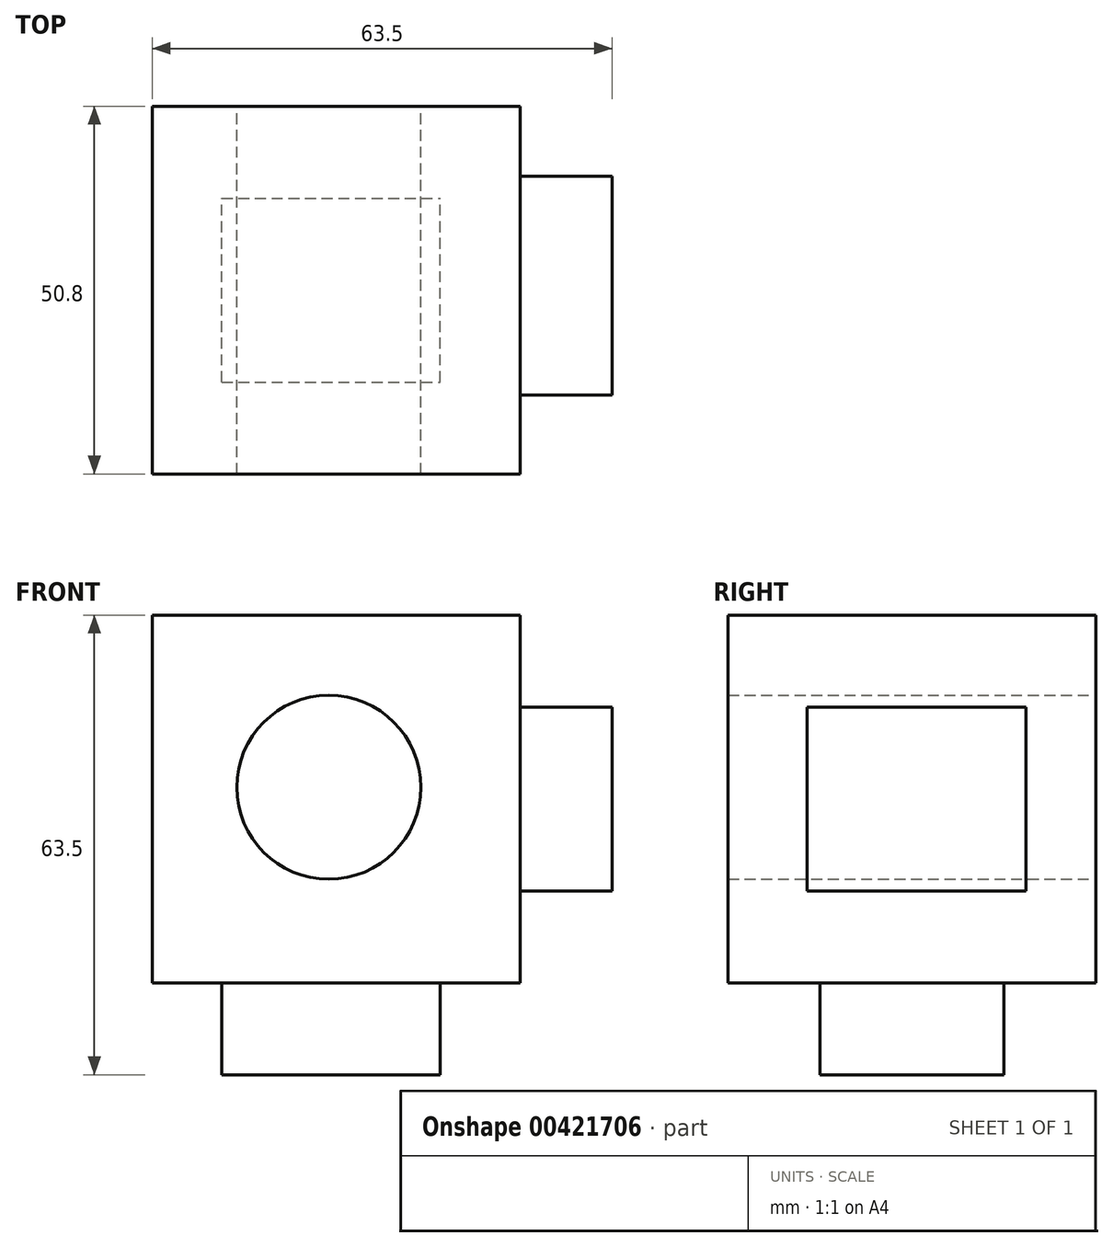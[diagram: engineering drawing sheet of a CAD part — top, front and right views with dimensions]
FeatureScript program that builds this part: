
annotation { "Feature Type Name" : "Feature", "Feature Type Description" : "" }
export const myFeature = defineFeature(function(context is Context, id is Id, definition is map)
    precondition{}
    {
        {
            var Q0;
            Q0=qCreatedBy(makeId("Front.planeOp"),FACE);
            var sketch = newSketch(context, id + "F0", { "sketchPlane" : qUnion([Q0])});
            skLineSegment(sketch, "E0.bottom", {"start": v(0, 0) * mm, "end": v(50.8, 0) * mm});
            skLineSegment(sketch, "E0.top", {"start": v(0, 50.8) * mm, "end": v(50.8, 50.8) * mm});
            skLineSegment(sketch, "E0.left", {"start": v(0, 0) * mm, "end": v(0, 50.8) * mm});
            skLineSegment(sketch, "E0.right", {"start": v(50.8, 0) * mm, "end": v(50.8, 50.8) * mm});
            skSolve(sketch);
        }
        {
            var Q0;
            Q0=makeQuery(id+"F0.imprint","IMPRINT",FACE,{"disambiguationData":[TD([[makeQuery(id+"F0.imprint","IMPRINT",EDGE,{"derivedFrom":sQuery(id+"F0.wireOp",EDGE,"E0.bottom")}),1.0]])]});
            var sketch = newSketch(context, id + "F1", { "sketchPlane" : qUnion([Q0])});
            skCircle(sketch, "E1", {"center": v(24.37, 27) * mm, "radius": 12.7 * mm});
            skSolve(sketch);
        }
        {
            var Q0;
            Q0=makeQuery(id+"F1.imprint","IMPRINT",FACE,{"disambiguationData":[TD([[makeQuery(id+"F1.imprint","IMPRINT",EDGE,{"derivedFrom":sQuery(id+"F1.wireOp",EDGE,"E1")}),-1.0]])]});
            extrude(context, id + "F2", {"entities" : qUnion([Q0]), "depth" : 50.8 * mm});
        }
        {
            var Q0;
            Q0=makeQuery(id+"F2.opExtrude","SWEPT_FACE",FACE,{"disambiguationData":[OSD([sQuery(id+"F0.wireOp",EDGE,"E0.bottom")])]});
            var sketch = newSketch(context, id + "F3", { "sketchPlane" : qUnion([Q0])});
            skLineSegment(sketch, "E2.bottom", {"start": v(9.6, 38.1) * mm, "end": v(39.75, 38.1) * mm});
            skLineSegment(sketch, "E2.top", {"start": v(9.6, 12.7) * mm, "end": v(39.75, 12.7) * mm});
            skLineSegment(sketch, "E2.left", {"start": v(9.6, 38.1) * mm, "end": v(9.6, 12.7) * mm});
            skLineSegment(sketch, "E2.right", {"start": v(39.75, 38.1) * mm, "end": v(39.75, 12.7) * mm});
            skSolve(sketch);
        }
        {
            var Q0;
            Q0=makeQuery(id+"F3.imprint","IMPRINT",FACE,{"disambiguationData":[TD([[makeQuery(id+"F3.imprint","IMPRINT",EDGE,{"derivedFrom":sQuery(id+"F3.wireOp",EDGE,"E2.bottom")}),-1.0]])]});
            extrude(context, id + "F4", {"entities" : qUnion([Q0]), "operationType" : NewBodyOperationType.ADD, "depth" : 12.7 * mm});
        }
        {
            var Q0;
            Q0=makeQuery(id+"F2.opExtrude","SWEPT_FACE",FACE,{"disambiguationData":[OSD([sQuery(id+"F0.wireOp",EDGE,"E0.right")])]});
            var sketch = newSketch(context, id + "F5", { "sketchPlane" : qUnion([Q0])});
            skLineSegment(sketch, "E3.bottom", {"start": v(-39.88, 38.1) * mm, "end": v(-9.67, 38.1) * mm});
            skLineSegment(sketch, "E3.top", {"start": v(-39.88, 12.7) * mm, "end": v(-9.67, 12.7) * mm});
            skLineSegment(sketch, "E3.left", {"start": v(-39.88, 38.1) * mm, "end": v(-39.88, 12.7) * mm});
            skLineSegment(sketch, "E3.right", {"start": v(-9.67, 38.1) * mm, "end": v(-9.67, 12.7) * mm});
            skSolve(sketch);
        }
        {
            var Q0;
            Q0=makeQuery(id+"F5.imprint","IMPRINT",FACE,{"disambiguationData":[TD([[makeQuery(id+"F5.imprint","IMPRINT",EDGE,{"derivedFrom":sQuery(id+"F5.wireOp",EDGE,"E3.bottom")}),-1.0]])]});
            extrude(context, id + "F6", {"entities" : qUnion([Q0]), "operationType" : NewBodyOperationType.ADD, "depth" : 12.7 * mm});
        }
    });
